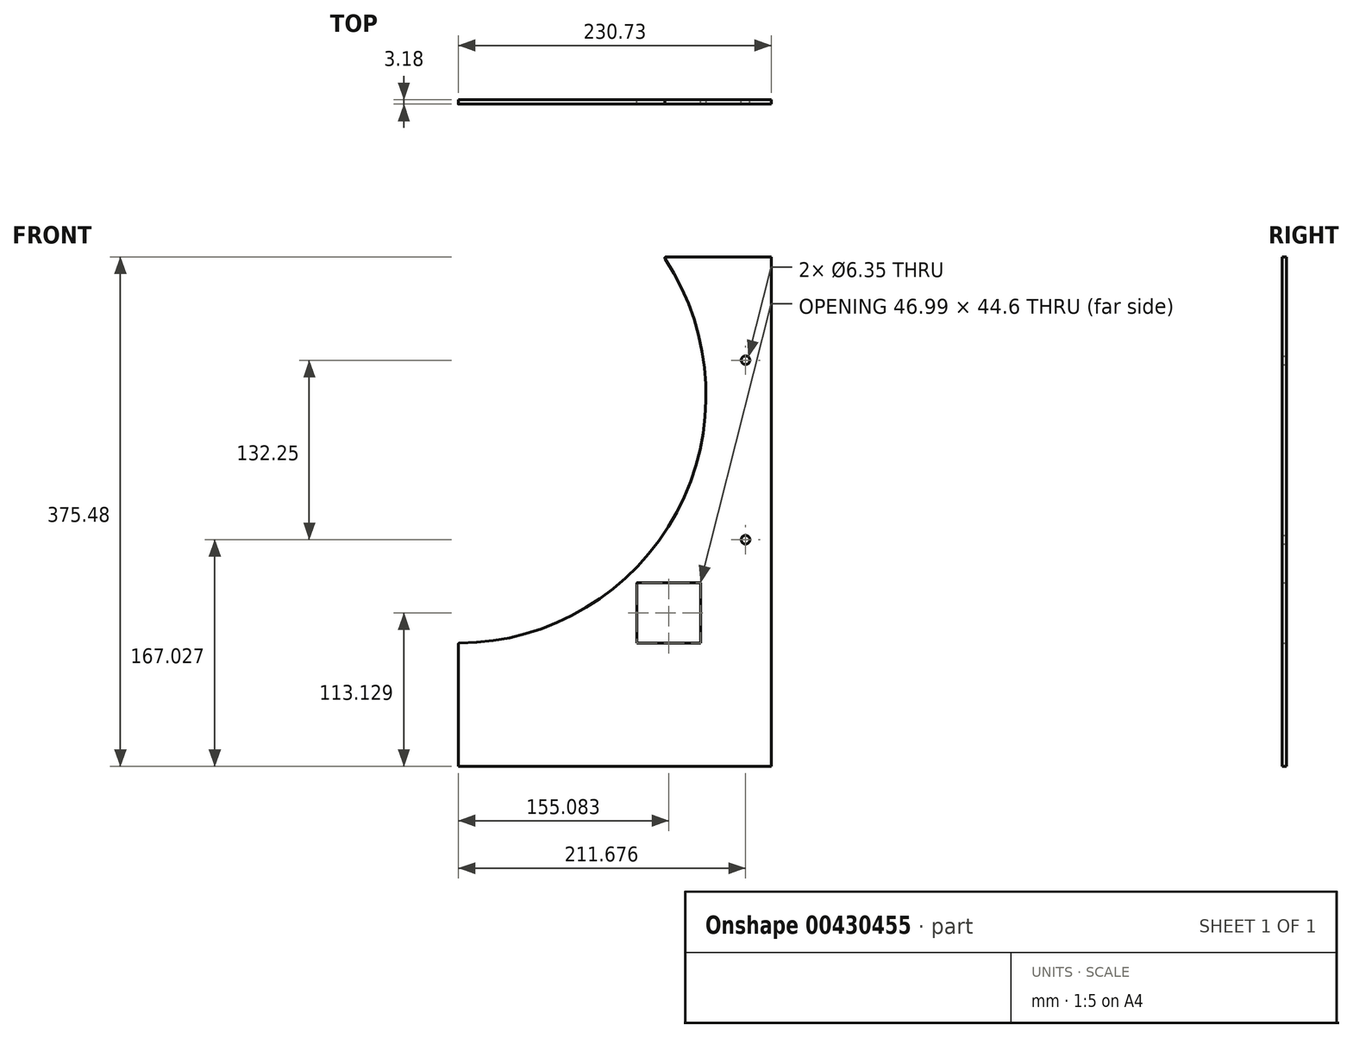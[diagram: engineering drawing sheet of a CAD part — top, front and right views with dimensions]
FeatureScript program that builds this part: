
annotation { "Feature Type Name" : "Feature", "Feature Type Description" : "" }
export const myFeature = defineFeature(function(context is Context, id is Id, definition is map)
    precondition{}
    {
        {
            var Q0;
            Q0=qCreatedBy(makeId("Front.planeOp"),FACE);
            var sketch = newSketch(context, id + "F0", { "sketchPlane" : qUnion([Q0])});
            skArc(sketch, "E0", {"start": v(0, -182.56) * mm, "mid": v(161.2, -85.7) * mm, "end": v(151.35, 102.09) * mm});
            skCircle(sketch, "E1", {"center": v(0, 0) * mm, "radius": 61.91 * mm, "construction": true});
            skLineSegment(sketch, "E2", {"start": v(0, 0) * mm, "end": v(0, -298.83) * mm, "construction": true});
            skLineSegment(sketch, "E3", {"start": v(0, -182.56) * mm, "end": v(131.59, -182.56) * mm, "construction": true});
            skLineSegment(sketch, "E4", {"start": v(230.73, -182.56) * mm, "end": v(230.73, 102.09) * mm});
            skLineSegment(sketch, "E5", {"start": v(230.73, 102.09) * mm, "end": v(151.35, 102.09) * mm});
            skLineSegment(sketch, "E6", {"start": v(0, 0) * mm, "end": v(377.6, 0) * mm, "construction": true});
            skLineSegment(sketch, "E7", {"start": v(182.56, 0) * mm, "end": v(151.35, 102.09) * mm, "construction": true});
            skLineSegment(sketch, "E8", {"start": v(182.56, 0) * mm, "end": v(182.56, 254) * mm, "construction": true});
            skCircle(sketch, "E9", {"center": v(173.38, 82.7) * mm, "radius": 3.18 * mm, "construction": true});
            skCircle(sketch, "E10.1.0", {"center": v(191.56, 14.24) * mm, "radius": 3.18 * mm, "construction": true});
            skCircle(sketch, "E10.2.0", {"center": v(183.7, -56.16) * mm, "radius": 3.18 * mm, "construction": true});
            skCircle(sketch, "E10.3.0", {"center": v(150.85, -118.92) * mm, "radius": 3.18 * mm, "construction": true});
            skCircle(sketch, "E10.4.0", {"center": v(97.5, -165.5) * mm, "radius": 3.18 * mm, "construction": true});
            skLineSegment(sketch, "E10.anchor1", {"start": v(0, 0) * mm, "end": v(173.38, 82.7) * mm, "construction": true});
            skLineSegment(sketch, "E10.anchor2", {"start": v(0, 0) * mm, "end": v(97.5, -165.5) * mm, "construction": true});
            skLineSegment(sketch, "E11.bottom", {"start": v(132.22, -137.96) * mm, "end": v(177.94, -137.96) * mm});
            skLineSegment(sketch, "E11.left", {"start": v(131.59, -138.6) * mm, "end": v(131.59, -182.56) * mm});
            skLineSegment(sketch, "E11.right", {"start": v(178.58, -138.6) * mm, "end": v(178.58, -182.56) * mm});
            skLineSegment(sketch, "E12", {"start": v(155.08, -137.96) * mm, "end": v(155.08, -182.56) * mm, "construction": true});
            skPoint(sketch, "E13", {"position": v(155.08, -160.26) * mm});
            skLineSegment(sketch, "E14.trimOffspring", {"start": v(178.58, -182.56) * mm, "end": v(230.73, -182.56) * mm, "construction": true});
            skPoint(sketch, "E15.visualSharp", {"position": v(131.59, -137.96) * mm});
            skArc(sketch, "E15.filletArc", {"start": v(132.22, -137.96) * mm, "mid": v(131.77, -138.15) * mm, "end": v(131.59, -138.6) * mm});
            skPoint(sketch, "E16.visualSharp", {"position": v(178.58, -137.96) * mm});
            skArc(sketch, "E16.filletArc", {"start": v(178.58, -138.6) * mm, "mid": v(178.4, -138.15) * mm, "end": v(177.94, -137.96) * mm});
            skLineSegment(sketch, "E17", {"start": v(211.68, 102.09) * mm, "end": v(211.68, -182.56) * mm, "construction": true});
            skLineSegment(sketch, "E18", {"start": v(230.73, 25.89) * mm, "end": v(180.72, 25.89) * mm, "construction": true});
            skLineSegment(sketch, "E19", {"start": v(148.38, -106.36) * mm, "end": v(230.73, -106.36) * mm, "construction": true});
            skCircle(sketch, "E20", {"center": v(211.68, -106.36) * mm, "radius": 3.18 * mm});
            skCircle(sketch, "E21", {"center": v(211.68, 25.89) * mm, "radius": 3.18 * mm});
            skLineSegment(sketch, "E22", {"start": v(0, 0) * mm, "end": v(151.35, 102.09) * mm, "construction": true});
            skLineSegment(sketch, "E23", {"start": v(0, -182.56) * mm, "end": v(0, -273.4) * mm});
            skLineSegment(sketch, "E24", {"start": v(0, -273.4) * mm, "end": v(230.73, -273.4) * mm});
            skLineSegment(sketch, "E25", {"start": v(230.73, -273.4) * mm, "end": v(230.73, -182.56) * mm});
            skLineSegment(sketch, "E26", {"start": v(131.59, -182.56) * mm, "end": v(178.58, -182.56) * mm});
            skSolve(sketch);
        }
        {
            var Q0;
            Q0 = qSketchRegion(id + "F0", true);
            extrude(context, id + "F1", {"entities" : qUnion([Q0]), "depth" : 3.17 * mm});
        }
        {
            var Q0;
            Q0=makeQuery(id+"F1.opExtrude","CAP_FACE",FACE,{"disambiguationData":[OSD([sQuery(id+"F0.wireOp",EDGE,"E0"),sQuery(id+"F0.wireOp",EDGE,"E3"),sQuery(id+"F0.wireOp",EDGE,"E4"),sQuery(id+"F0.wireOp",EDGE,"E5"),sQuery(id+"F0.wireOp",EDGE,"E11.bottom"),sQuery(id+"F0.wireOp",EDGE,"E11.left"),sQuery(id+"F0.wireOp",EDGE,"E11.right"),sQuery(id+"F0.wireOp",EDGE,"E14.trimOffspring"),sQuery(id+"F0.wireOp",EDGE,"E15.filletArc"),sQuery(id+"F0.wireOp",EDGE,"E16.filletArc")])],"isStart":false});
            var sketch = newSketch(context, id + "F2", { "sketchPlane" : qUnion([Q0])});
            skLineSegment(sketch, "E27", {"start": v(86.22, -160.92) * mm, "end": v(87, -162.32) * mm});
            skLineSegment(sketch, "E28", {"start": v(87, -162.32) * mm, "end": v(84.93, -163.45) * mm});
            skLineSegment(sketch, "E29", {"start": v(84.93, -163.45) * mm, "end": v(86.58, -166.46) * mm});
            skLineSegment(sketch, "E30", {"start": v(86.58, -166.46) * mm, "end": v(88.64, -165.33) * mm});
            skLineSegment(sketch, "E31", {"start": v(88.64, -165.33) * mm, "end": v(89.52, -166.93) * mm});
            skLineSegment(sketch, "E32", {"start": v(89.52, -166.93) * mm, "end": v(92.64, -165.22) * mm});
            skLineSegment(sketch, "E33", {"start": v(92.64, -165.22) * mm, "end": v(91.76, -163.62) * mm});
            skLineSegment(sketch, "E34", {"start": v(91.76, -163.62) * mm, "end": v(93.82, -162.49) * mm});
            skLineSegment(sketch, "E35", {"start": v(93.82, -162.49) * mm, "end": v(92.17, -159.48) * mm});
            skLineSegment(sketch, "E36", {"start": v(92.17, -159.48) * mm, "end": v(90.11, -160.61) * mm});
            skLineSegment(sketch, "E37", {"start": v(90.11, -160.61) * mm, "end": v(89.34, -159.2) * mm});
            skLineSegment(sketch, "E38", {"start": v(164.06, 80.1) * mm, "end": v(165.5, 80.78) * mm});
            skLineSegment(sketch, "E39", {"start": v(165.5, 80.78) * mm, "end": v(164.49, 82.9) * mm});
            skLineSegment(sketch, "E40", {"start": v(164.49, 82.9) * mm, "end": v(167.59, 84.38) * mm});
            skLineSegment(sketch, "E41", {"start": v(167.59, 84.38) * mm, "end": v(168.6, 82.26) * mm});
            skLineSegment(sketch, "E42", {"start": v(168.6, 82.26) * mm, "end": v(170.25, 83.04) * mm});
            skLineSegment(sketch, "E43", {"start": v(170.25, 83.04) * mm, "end": v(171.78, 79.83) * mm});
            skLineSegment(sketch, "E44", {"start": v(171.78, 79.83) * mm, "end": v(170.12, 79.04) * mm});
            skLineSegment(sketch, "E45", {"start": v(170.12, 79.04) * mm, "end": v(171.14, 76.92) * mm});
            skLineSegment(sketch, "E46", {"start": v(171.14, 76.92) * mm, "end": v(168.04, 75.45) * mm});
            skLineSegment(sketch, "E47", {"start": v(168.04, 75.45) * mm, "end": v(167.03, 77.57) * mm});
            skLineSegment(sketch, "E48", {"start": v(167.03, 77.57) * mm, "end": v(165.58, 76.88) * mm});
            skSolve(sketch);
        }
        {
            var Q0;
            Q0=makeQuery(id+"F1.opExtrude","SWEPT_EDGE",EDGE,{"disambiguationData":[OSD([sQuery(id+"F0.wireOp",EDGE,"E0"),sQuery(id+"F0.wireOp",EDGE,"E5")])]});
            var Q1;
            Q1=makeQuery(id+"F1.opExtrude","SWEPT_EDGE",EDGE,{"disambiguationData":[OSD([sQuery(id+"F0.wireOp",EDGE,"E0"),sQuery(id+"F0.wireOp",EDGE,"E3")])]});
            fillet(context, id + "F3", {"entities" : qUnion([Q0, Q1]), "radius" : 1.02 * mm, "tangentPropagation" : true, "allowEdgeOverflow" : false});
        }
    });
